# Revit family: DC_Holyoake_LowLeakageDamper_HCD-150-MOT_12
name_source: partatom
category: Duct Accessories
revit_build: Autodesk Revit 2013 (Build: 20120221_2030(x64)
units: mm (PartAtom-declared; Revit-internal decimal feet)

## types (1)
- Variable Width & Height
    3D Visibility ON OFF = No
    Description = Motorised Low Leakage Volume Control Dampers shall be Holyoake Model HCD-150-MOT.Motorised Low Leakage Volume Control Dampers shall be of 6063 T5 extruded aluminium construction, with a 150mm Flanged Frame incorporating pre-punched corner slots for Duct Flange mounting or Channel Frame suitable for fixing inside ductwork. Low Leakage Volume Control Dampers shall incorporate single piece Airfoil Blades, fitted with self inflating edge seals and flexible aluminium side seals. Low Leakage Volume Control Dampers shall be fitted with 11mm Hexagonal shafts and shall rotate in two piece Acetal self lubricating bearings.
    Holyoake Product Range = Holyoake Motorised Volume Control Damper Elevated Temperature
    Manufacturer = Holyoake
    Material Body = Holyoake-Aluminium
    Material Face = Holyoake-Aluminium
    Model = HCD-150-MOTORISED
    Static Pressure Max / sqm = 2000 Pa
    Static Pressure Min / sqm = 10 Pa
    Type Comments = Low Leakage Motorised Volume Control Damper
    URL = http://www.holyoake.com

## geometry (parser evidence)
native form markers: Blend x12, Extrusion x6, Sweep x3
no freeform markers — native parametric forms only
